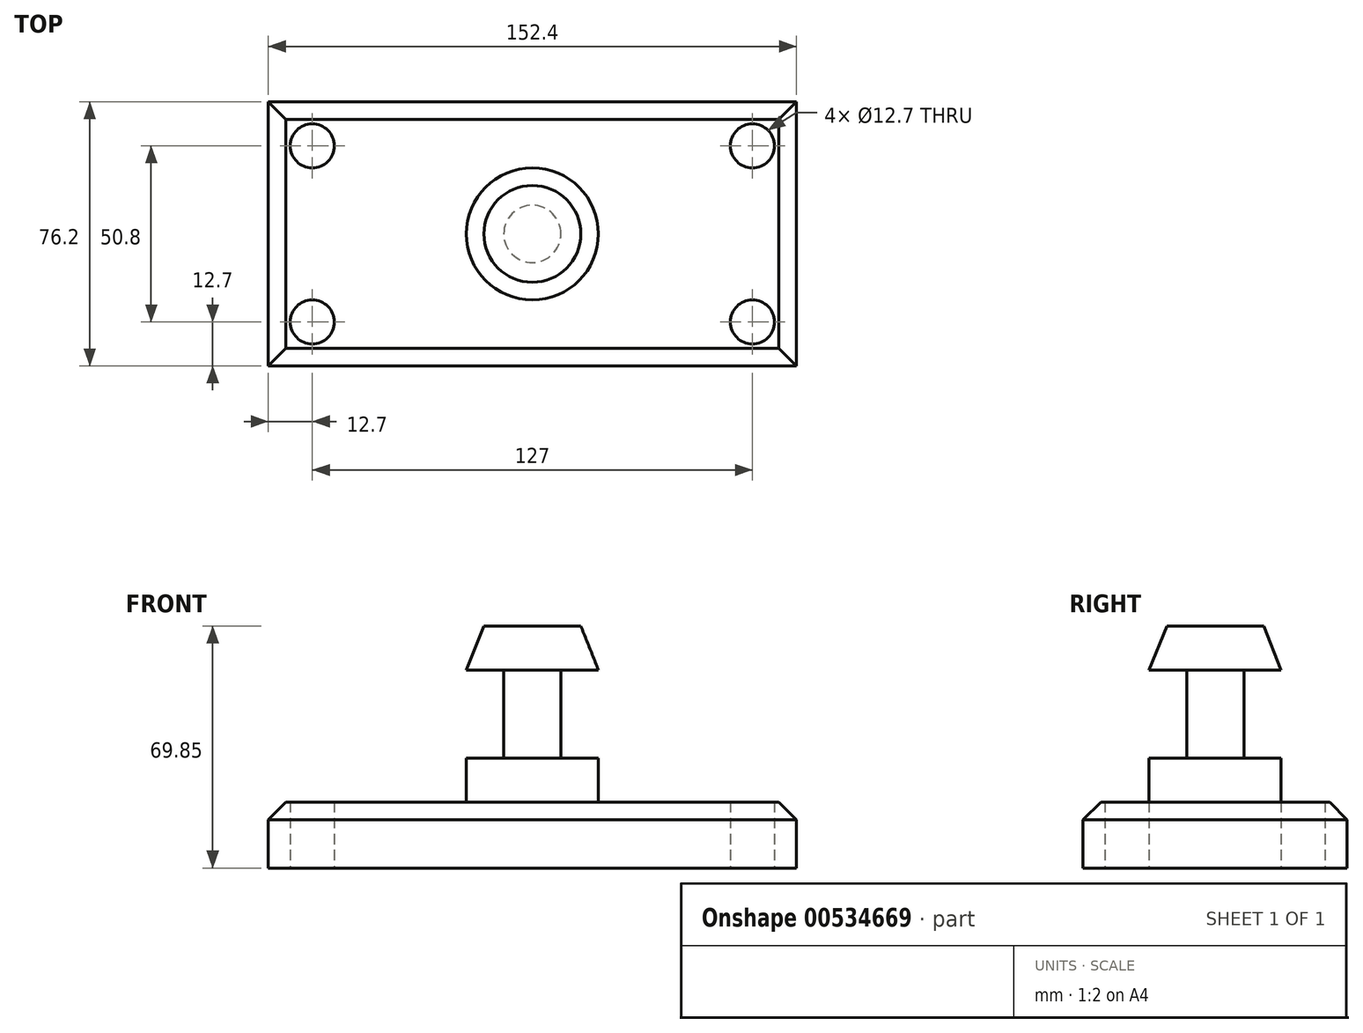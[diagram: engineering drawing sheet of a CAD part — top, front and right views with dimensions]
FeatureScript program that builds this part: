
annotation { "Feature Type Name" : "Feature", "Feature Type Description" : "" }
export const myFeature = defineFeature(function(context is Context, id is Id, definition is map)
    precondition{}
    {
        {
            var Q0;
            Q0=qCreatedBy(makeId("Top.planeOp"),FACE);
            var sketch = newSketch(context, id + "F0", { "sketchPlane" : qUnion([Q0])});
            skLineSegment(sketch, "E0.bottom", {"start": v(76.2, -38.1) * mm, "end": v(-76.2, -38.1) * mm});
            skLineSegment(sketch, "E0.top", {"start": v(76.2, 38.1) * mm, "end": v(-76.2, 38.1) * mm});
            skLineSegment(sketch, "E0.left", {"start": v(76.2, -38.1) * mm, "end": v(76.2, 38.1) * mm});
            skLineSegment(sketch, "E0.right", {"start": v(-76.2, -38.1) * mm, "end": v(-76.2, 38.1) * mm});
            skPoint(sketch, "E0.middle", {"position": v(0, 0) * mm});
            skSolve(sketch);
        }
        {
            var Q0;
            Q0=makeQuery(id+"F0.imprint","IMPRINT",FACE,{"disambiguationData":[TD([[makeQuery(id+"F0.imprint","IMPRINT",EDGE,{"derivedFrom":sQuery(id+"F0.wireOp",EDGE,"E0.bottom")}),-1.0]])]});
            extrude(context, id + "F1", {"entities" : qUnion([Q0]), "depth" : 19.05 * mm, "offsetDistance" : 25.4 * mm});
        }
        {
            var Q0;
            Q0=qCreatedBy(makeId("Top.planeOp"),FACE);
            var sketch = newSketch(context, id + "F2", { "sketchPlane" : qUnion([Q0])});
            skCircle(sketch, "E1", {"center": v(-63.5, 25.4) * mm, "radius": 6.35 * mm});
            skCircle(sketch, "E2", {"center": v(63.5, -25.4) * mm, "radius": 6.35 * mm});
            skCircle(sketch, "E3", {"center": v(63.5, 25.4) * mm, "radius": 6.35 * mm});
            skCircle(sketch, "E4", {"center": v(-63.5, -25.4) * mm, "radius": 6.35 * mm});
            skSolve(sketch);
        }
        {
            var Q0;
            Q0 = qSketchRegion(id + "F2", true);
            extrude(context, id + "F3", {"entities" : qUnion([Q0]), "operationType" : NewBodyOperationType.REMOVE, "endBound" : BoundingType.THROUGH_ALL, "depth" : 50.8 * mm, "offsetDistance" : 25.4 * mm});
        }
        {
            var Q0;
            Q0=qCreatedBy(makeId("Front.planeOp"),FACE);
            var sketch = newSketch(context, id + "F4", { "sketchPlane" : qUnion([Q0])});
            skLineSegment(sketch, "E5.bottom", {"start": v(0, 69.85) * mm, "end": v(19.05, 69.85) * mm});
            skLineSegment(sketch, "E5.top", {"start": v(0, 19.05) * mm, "end": v(19.05, 19.05) * mm});
            skLineSegment(sketch, "E5.left", {"start": v(0, 69.85) * mm, "end": v(0, 19.05) * mm});
            skLineSegment(sketch, "E5.right", {"start": v(19.05, 69.85) * mm, "end": v(19.05, 19.05) * mm});
            skSolve(sketch);
        }
        {
            var Q0;
            Q0=makeQuery(id+"F4.imprint","IMPRINT",FACE,{"disambiguationData":[TD([[makeQuery(id+"F4.imprint","IMPRINT",EDGE,{"derivedFrom":sQuery(id+"F4.wireOp",EDGE,"E5.bottom")}),-1.0]])]});
            var Q1;
            Q1=sQuery(id+"F4.wireOp",EDGE,"E5.left");
            revolve(context, id + "F5", {"operationType" : NewBodyOperationType.ADD, "entities" : qUnion([Q0]), "axis" : qUnion([Q1]), "revolveType" : RevolveType.FULL});
        }
        {
            var Q0;
            Q0=makeQuery(id+"F1.opExtrude","CAP_EDGE",EDGE,{"disambiguationData":[OSD([sQuery(id+"F0.wireOp",EDGE,"E0.bottom")])],"isStart":false});
            var Q1;
            Q1=makeQuery(id+"F1.opExtrude","CAP_EDGE",EDGE,{"disambiguationData":[OSD([sQuery(id+"F0.wireOp",EDGE,"E0.right")])],"isStart":false});
            var Q2;
            Q2=makeQuery(id+"F1.opExtrude","CAP_EDGE",EDGE,{"disambiguationData":[OSD([sQuery(id+"F0.wireOp",EDGE,"E0.top")])],"isStart":false});
            var Q3;
            Q3=makeQuery(id+"F1.opExtrude","CAP_EDGE",EDGE,{"disambiguationData":[OSD([sQuery(id+"F0.wireOp",EDGE,"E0.left")])],"isStart":false});
            chamfer(context, id + "F6", {"entities" : qUnion([Q0, Q1, Q2, Q3]), "width" : 5.08 * mm, "tangentPropagation" : true});
        }
        {
            var Q0;
            Q0=qCreatedBy(makeId("Front.planeOp"),FACE);
            var sketch = newSketch(context, id + "F7", { "sketchPlane" : qUnion([Q0])});
            skLineSegment(sketch, "E6.bottom", {"start": v(19.05, 57.15) * mm, "end": v(8.25, 57.15) * mm});
            skLineSegment(sketch, "E6.top", {"start": v(19.05, 31.75) * mm, "end": v(8.26, 31.75) * mm});
            skLineSegment(sketch, "E6.left", {"start": v(19.05, 57.15) * mm, "end": v(19.05, 31.75) * mm});
            skLineSegment(sketch, "E6.right", {"start": v(8.25, 57.15) * mm, "end": v(8.26, 31.75) * mm});
            skSolve(sketch);
        }
        {
            var Q0;
            Q0 = qSketchRegion(id + "F7", true);
            var Q1;
            Q1=makeQuery(id+"F5.opRevolve","SWEPT_FACE",FACE,{"disambiguationData":[OSD([sQuery(id+"F4.wireOp",EDGE,"E5.right")])]});
            revolve(context, id + "F8", {"operationType" : NewBodyOperationType.REMOVE, "entities" : qUnion([Q0]), "axis" : qUnion([Q1]), "revolveType" : RevolveType.FULL, "oppositeDirection" : true});
        }
        {
            var Q0;
            Q0=makeQuery(id+"F5.opRevolve","SWEPT_EDGE",EDGE,{"disambiguationData":[OSD([sQuery(id+"F4.wireOp",EDGE,"E5.bottom"),sQuery(id+"F4.wireOp",EDGE,"E5.right")])]});
            chamfer(context, id + "F9", {"entities" : qUnion([Q0]), "chamferType" : ChamferType.TWO_OFFSETS, "width1" : 5.08 * mm, "oppositeDirection" : false, "width2" : 12.7 * mm, "tangentPropagation" : true});
        }
    });
